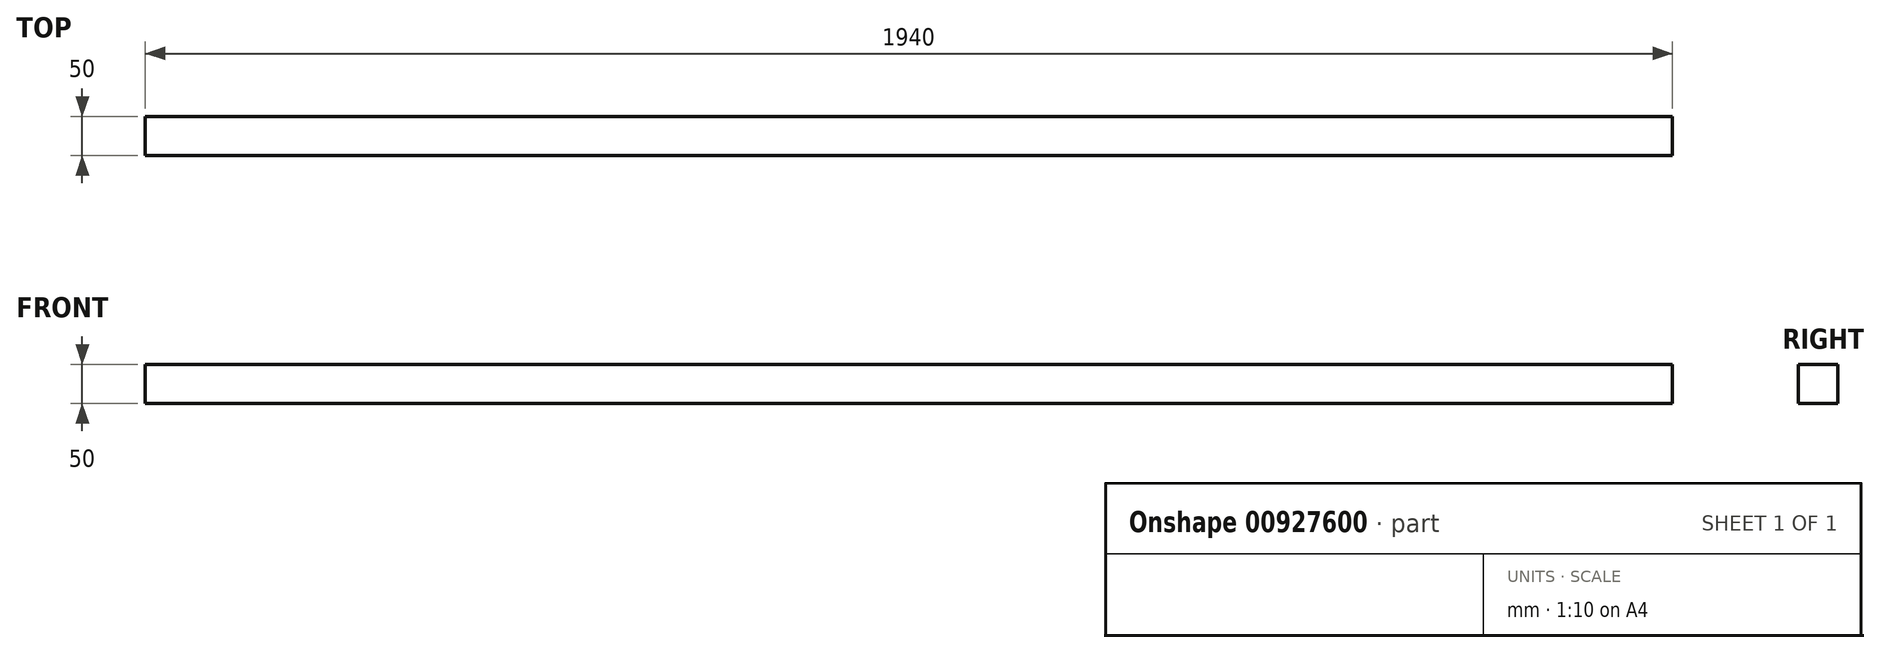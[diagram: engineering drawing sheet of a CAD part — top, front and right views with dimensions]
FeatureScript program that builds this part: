
annotation { "Feature Type Name" : "Feature", "Feature Type Description" : "" }
export const myFeature = defineFeature(function(context is Context, id is Id, definition is map)
    precondition{}
    {
        {
            var Q0;
            Q0=qCreatedBy(makeId("Right.planeOp"),FACE);
            var sketch = newSketch(context, id + "F0", { "sketchPlane" : qUnion([Q0])});
            skLineSegment(sketch, "E0.bottom", {"start": v(-50, 50) * mm, "end": v(0, 50) * mm});
            skLineSegment(sketch, "E0.top", {"start": v(-50, 0) * mm, "end": v(0, 0) * mm});
            skLineSegment(sketch, "E0.left", {"start": v(-50, 50) * mm, "end": v(-50, 0) * mm});
            skLineSegment(sketch, "E0.right", {"start": v(0, 50) * mm, "end": v(0, 0) * mm});
            skSolve(sketch);
        }
        {
            var Q0;
            Q0=makeQuery(id+"F0.imprint","IMPRINT",FACE,{"disambiguationData":[TD([[makeQuery(id+"F0.imprint","IMPRINT",EDGE,{"derivedFrom":sQuery(id+"F0.wireOp",EDGE,"E0.bottom")}),-1.0]])]});
            extrude(context, id + "F1", {"entities" : qUnion([Q0]), "depth" : 1940 * mm, "offsetDistance" : 25 * mm});
        }
    });
